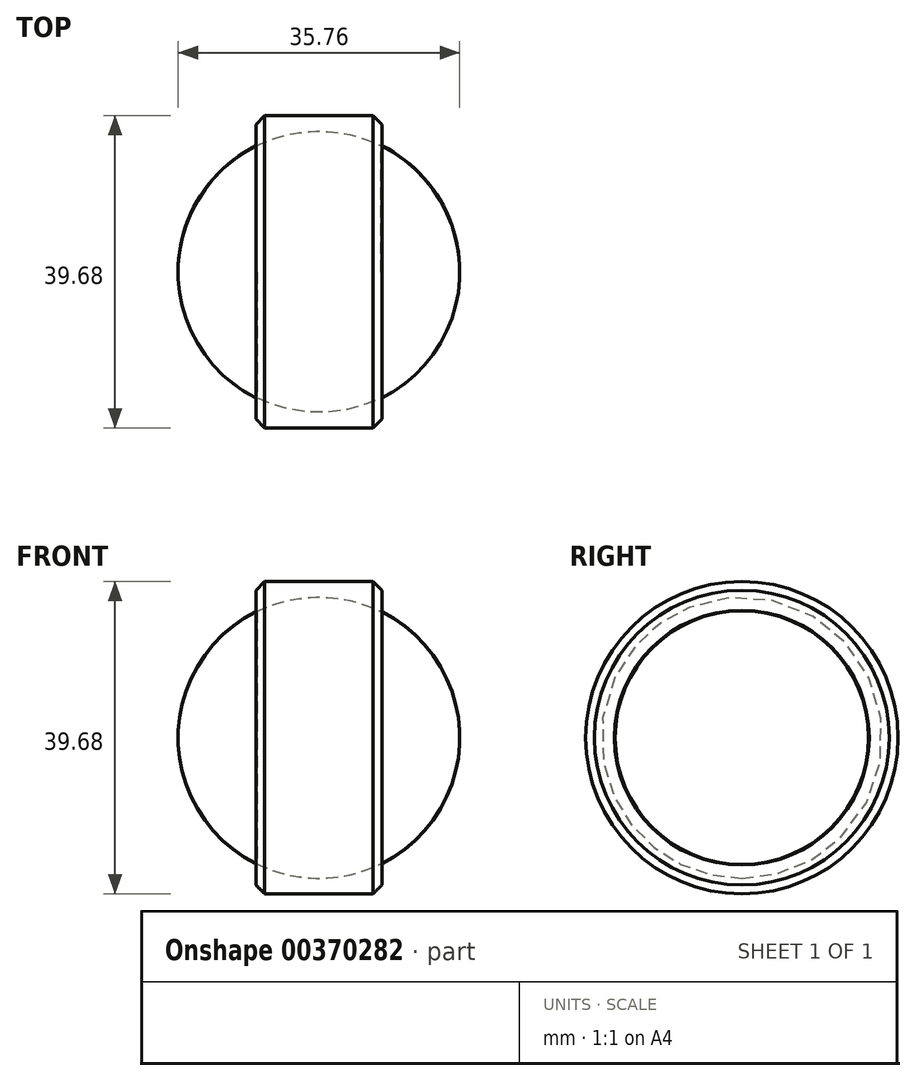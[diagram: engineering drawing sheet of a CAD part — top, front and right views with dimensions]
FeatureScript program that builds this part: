
annotation { "Feature Type Name" : "Feature", "Feature Type Description" : "" }
export const myFeature = defineFeature(function(context is Context, id is Id, definition is map)
    precondition{}
    {
        {
            var Q0;
            Q0=qCreatedBy(makeId("Front.planeOp"),FACE);
            var sketch = newSketch(context, id + "F0", { "sketchPlane" : qUnion([Q0])});
            skLineSegment(sketch, "E0.top", {"start": v(-8, 19.84) * mm, "end": v(8, 19.84) * mm});
            skLineSegment(sketch, "E1", {"start": v(-8, 19.84) * mm, "end": v(-8, 16.02) * mm});
            skLineSegment(sketch, "E2", {"start": v(8, 19.84) * mm, "end": v(8, 16.02) * mm});
            skArc(sketch, "E3", {"start": v(8, 16.02) * mm, "mid": v(0, 17.91) * mm, "end": v(-8, 16.02) * mm});
            skLineSegment(sketch, "E4", {"start": v(0, 0) * mm, "end": v(-13.04, 0) * mm, "construction": true});
            skLineSegment(sketch, "E5", {"start": v(-8, 16.02) * mm, "end": v(-8, 0) * mm, "construction": true});
            skLineSegment(sketch, "E6", {"start": v(8, 16.02) * mm, "end": v(8, 0) * mm, "construction": true});
            skLineSegment(sketch, "E7", {"start": v(0, 0) * mm, "end": v(0, 17.91) * mm, "construction": true});
            skSolve(sketch);
        }
        {
            var Q0;
            Q0=qCreatedBy(makeId("Front.planeOp"),FACE);
            var sketch = newSketch(context, id + "F1", { "sketchPlane" : qUnion([Q0])});
            skLineSegment(sketch, "E8", {"start": v(-10.09, 0) * mm, "end": v(10.2, 0) * mm});
            skSolve(sketch);
        }
        {
            var Q0;
            Q0=makeQuery(id+"F0.imprint","IMPRINT",FACE,{"disambiguationData":[TD([[makeQuery(id+"F0.imprint","IMPRINT",EDGE,{"derivedFrom":sQuery(id+"F0.wireOp",EDGE,"E0.top")}),-1.0]])]});
            var Q1;
            Q1=sQuery(id+"F1.wireOp",EDGE,"E8");
            revolve(context, id + "F2", {"entities" : qUnion([Q0]), "axis" : qUnion([Q1]), "revolveType" : RevolveType.FULL});
        }
        {
            var Q0;
            Q0=makeQuery(id+"F2.opRevolve","SWEPT_EDGE",EDGE,{"disambiguationData":[OSD([sQuery(id+"F0.wireOp",EDGE,"E2"),sQuery(id+"F0.wireOp",EDGE,"E3")])]});
            var Q1;
            Q1=makeQuery(id+"F2.opRevolve","SWEPT_EDGE",EDGE,{"disambiguationData":[OSD([sQuery(id+"F0.wireOp",EDGE,"E1"),sQuery(id+"F0.wireOp",EDGE,"E3")])]});
            chamfer(context, id + "F3", {"entities" : qUnion([Q0, Q1]), "width" : 0.1 * mm, "tangentPropagation" : true});
        }
        {
            var Q0;
            Q0=makeQuery(id+"F2.opRevolve","SWEPT_EDGE",EDGE,{"disambiguationData":[OSD([sQuery(id+"F0.wireOp",EDGE,"E0.top"),sQuery(id+"F0.wireOp",EDGE,"E1")])]});
            var Q1;
            Q1=makeQuery(id+"F2.opRevolve","SWEPT_EDGE",EDGE,{"disambiguationData":[OSD([sQuery(id+"F0.wireOp",EDGE,"E0.top"),sQuery(id+"F0.wireOp",EDGE,"E2")])]});
            chamfer(context, id + "F4", {"entities" : qUnion([Q0, Q1]), "width" : 1.12 * mm, "tangentPropagation" : true});
        }
    });
